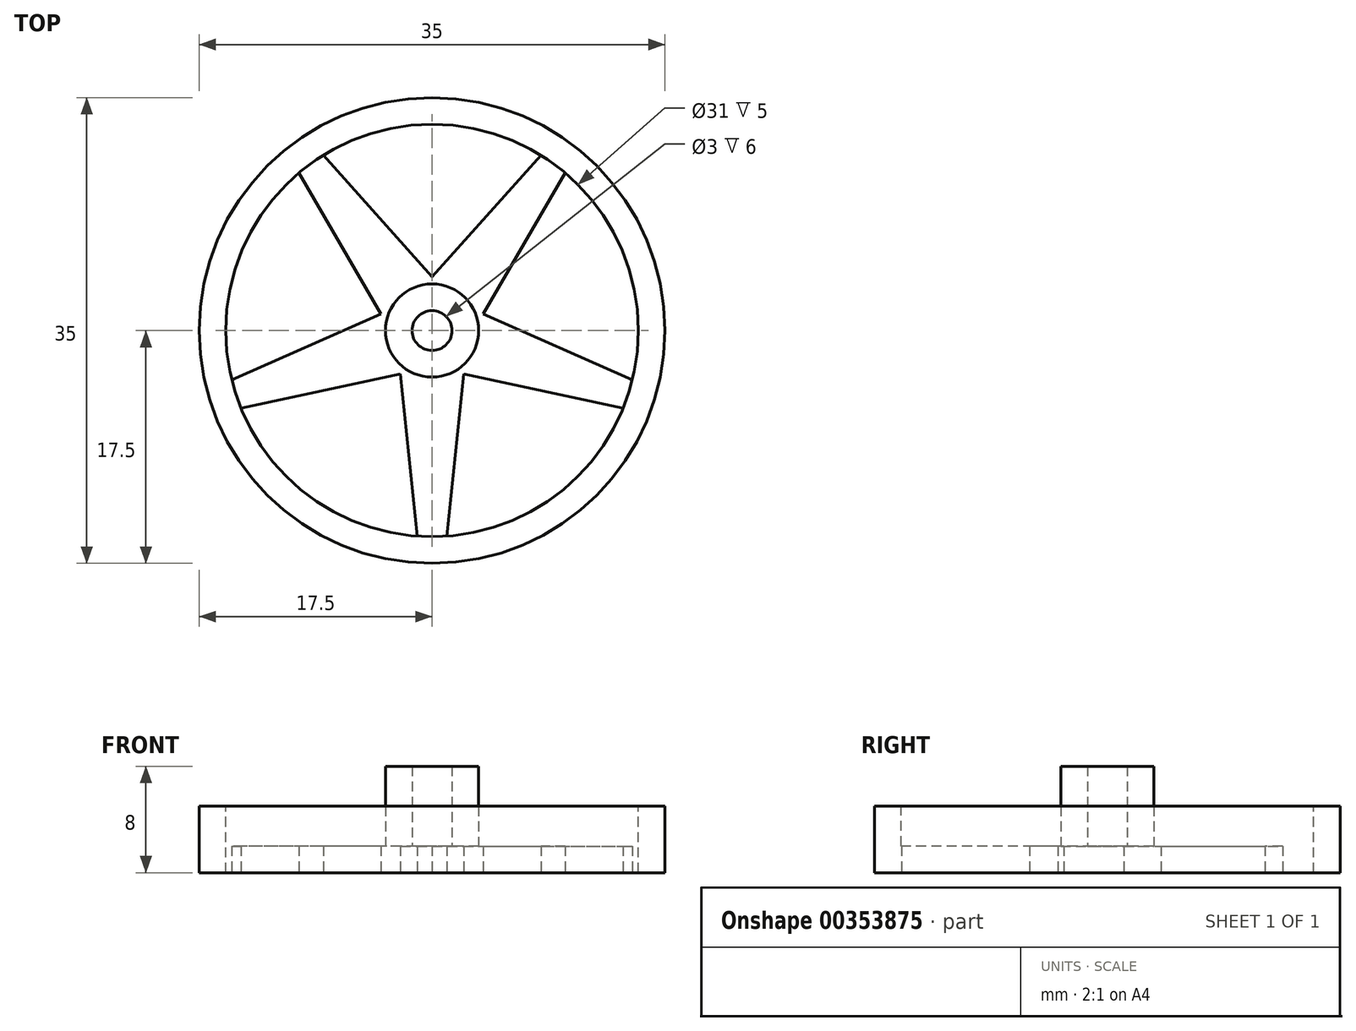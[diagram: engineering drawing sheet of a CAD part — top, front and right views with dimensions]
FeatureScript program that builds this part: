
annotation { "Feature Type Name" : "Feature", "Feature Type Description" : "" }
export const myFeature = defineFeature(function(context is Context, id is Id, definition is map)
    precondition{}
    {
        {
            var Q0;
            Q0=qCreatedBy(makeId("Top.planeOp"),FACE);
            var sketch = newSketch(context, id + "F0", { "sketchPlane" : qUnion([Q0])});
            skCircle(sketch, "E0", {"center": v(0, 0) * mm, "radius": 17.5 * mm});
            skSolve(sketch);
        }
        {
            var Q0;
            Q0=makeQuery(id+"F0.imprint","IMPRINT",FACE,{"disambiguationData":[TD([[makeQuery(id+"F0.imprint","IMPRINT",EDGE,{"derivedFrom":sQuery(id+"F0.wireOp",EDGE,"E0")}),1.0]])]});
            extrude(context, id + "F1", {"entities" : qUnion([Q0]), "depth" : 5 * mm});
        }
        {
            var Q0;
            Q0=makeQuery(id+"F1.opExtrude","CAP_FACE",FACE,{"disambiguationData":[OSD([sQuery(id+"F0.wireOp",EDGE,"E0")])],"isStart":false});
            var sketch = newSketch(context, id + "F2", { "sketchPlane" : qUnion([Q0])});
            skCircle(sketch, "E1", {"center": v(0, 0) * mm, "radius": 15.5 * mm});
            skSolve(sketch);
        }
        {
            var Q0;
            Q0=makeQuery(id+"F2.imprint","IMPRINT",FACE,{"disambiguationData":[TD([[makeQuery(id+"F2.imprint","IMPRINT",EDGE,{"derivedFrom":sQuery(id+"F2.wireOp",EDGE,"E1")}),1.0]])]});
            extrude(context, id + "F3", {"entities" : qUnion([Q0]), "operationType" : NewBodyOperationType.REMOVE, "oppositeDirection" : true, "depth" : 3 * mm});
        }
        {
            var Q0;
            Q0=makeQuery(id+"F3.boolean.opBoolean","COPY",FACE,{"derivedFrom":makeQuery(id+"F3.opExtrude","CAP_FACE",FACE,{"disambiguationData":[OSD([sQuery(id+"F2.wireOp",EDGE,"E1")])],"isStart":false})});
            var sketch = newSketch(context, id + "F4", { "sketchPlane" : qUnion([Q0])});
            skCircle(sketch, "E2", {"center": v(0, 0) * mm, "radius": 3.5 * mm});
            skCircle(sketch, "E3", {"center": v(0, 0) * mm, "radius": 1.5 * mm});
            skSolve(sketch);
        }
        {
            var Q0;
            Q0=makeQuery(id+"F4.imprint","IMPRINT",FACE,{"disambiguationData":[TD([[makeQuery(id+"F4.imprint","IMPRINT",EDGE,{"derivedFrom":sQuery(id+"F4.wireOp",EDGE,"E2")}),1.0]])]});
            extrude(context, id + "F5", {"entities" : qUnion([Q0]), "operationType" : NewBodyOperationType.ADD, "depth" : 6 * mm});
        }
        {
            var Q0;
            Q0=makeQuery(id+"F1.opExtrude","CAP_FACE",FACE,{"disambiguationData":[OSD([sQuery(id+"F0.wireOp",EDGE,"E0")])],"isStart":true});
            var sketch = newSketch(context, id + "F6", { "sketchPlane" : qUnion([Q0])});
            skCircle(sketch, "E4", {"center": v(0, 0) * mm, "radius": 3.5 * mm});
            skCircle(sketch, "E5", {"center": v(0, 0) * mm, "radius": 15.5 * mm});
            skLineSegment(sketch, "E6", {"start": v(-2.45, 2.5) * mm, "end": v(-1.12, 15.46) * mm});
            skLineSegment(sketch, "E7.MirrorCS", {"start": v(2.45, 2.5) * mm, "end": v(1.12, 15.46) * mm});
            skLineSegment(sketch, "E8.1.0", {"start": v(-1.62, 3.1) * mm, "end": v(-14.36, 5.85) * mm});
            skLineSegment(sketch, "E8.1.1", {"start": v(-3.13, -1.56) * mm, "end": v(-15.05, 3.7) * mm});
            skLineSegment(sketch, "E8.2.0", {"start": v(-3.45, -0.58) * mm, "end": v(-10, -11.85) * mm});
            skLineSegment(sketch, "E8.2.1", {"start": v(0.51, -3.46) * mm, "end": v(-8.18, -13.17) * mm});
            skLineSegment(sketch, "E8.3.0", {"start": v(-0.51, -3.46) * mm, "end": v(8.18, -13.17) * mm});
            skLineSegment(sketch, "E8.3.1", {"start": v(3.45, -0.58) * mm, "end": v(10, -11.85) * mm});
            skLineSegment(sketch, "E8.4.0", {"start": v(3.13, -1.56) * mm, "end": v(15.05, 3.7) * mm});
            skLineSegment(sketch, "E8.4.1", {"start": v(1.62, 3.1) * mm, "end": v(14.36, 5.85) * mm});
            skSolve(sketch);
        }
        {
            var Q0;
            {var subQ0=sQuery(id+"F6.wireOp",EDGE,"E6");var subQ1=sQuery(id+"F6.wireOp",EDGE,"E5");var subQ2=makeQuery(id+"F6.imprint","INTERSECT",VERTEX,{"derivedFrom":[subQ1,subQ0]});Q0=makeQuery(id+"F6.imprint","IMPRINT",FACE,{"disambiguationData":[TD([[makeQuery(id+"F6.imprint","IMPRINT",EDGE,{"disambiguationData":[TD([[subQ2,-1.0]])],"derivedFrom":subQ1}),1.0]])]});}
            var Q1;
            {var subQ0=sQuery(id+"F6.wireOp",EDGE,"E7.MirrorCS");var subQ1=sQuery(id+"F6.wireOp",EDGE,"E5");var subQ2=makeQuery(id+"F6.imprint","INTERSECT",VERTEX,{"derivedFrom":[subQ1,subQ0]});Q1=makeQuery(id+"F6.imprint","IMPRINT",FACE,{"disambiguationData":[TD([[makeQuery(id+"F6.imprint","IMPRINT",EDGE,{"disambiguationData":[TD([[subQ2,1.0]])],"derivedFrom":subQ1}),1.0]])]});}
            var Q2;
            {var subQ0=sQuery(id+"F6.wireOp",EDGE,"E8.3.1");var subQ1=sQuery(id+"F6.wireOp",EDGE,"E5");var subQ2=makeQuery(id+"F6.imprint","INTERSECT",VERTEX,{"derivedFrom":[subQ1,subQ0]});Q2=makeQuery(id+"F6.imprint","IMPRINT",FACE,{"disambiguationData":[TD([[makeQuery(id+"F6.imprint","IMPRINT",EDGE,{"disambiguationData":[TD([[subQ2,-1.0]])],"derivedFrom":subQ1}),1.0]])]});}
            var Q3;
            {var subQ0=sQuery(id+"F6.wireOp",EDGE,"E8.2.1");var subQ1=sQuery(id+"F6.wireOp",EDGE,"E5");var subQ2=makeQuery(id+"F6.imprint","INTERSECT",VERTEX,{"derivedFrom":[subQ1,subQ0]});Q3=makeQuery(id+"F6.imprint","IMPRINT",FACE,{"disambiguationData":[TD([[makeQuery(id+"F6.imprint","IMPRINT",EDGE,{"disambiguationData":[TD([[subQ2,-1.0]])],"derivedFrom":subQ1}),1.0]])]});}
            var Q4;
            {var subQ0=sQuery(id+"F6.wireOp",EDGE,"E8.1.1");var subQ1=sQuery(id+"F6.wireOp",EDGE,"E5");var subQ2=makeQuery(id+"F6.imprint","INTERSECT",VERTEX,{"derivedFrom":[subQ1,subQ0]});Q4=makeQuery(id+"F6.imprint","IMPRINT",FACE,{"disambiguationData":[TD([[makeQuery(id+"F6.imprint","IMPRINT",EDGE,{"disambiguationData":[TD([[subQ2,-1.0]])],"derivedFrom":subQ1}),1.0]])]});}
            extrude(context, id + "F7", {"entities" : qUnion([Q0, Q1, Q2, Q3, Q4]), "operationType" : NewBodyOperationType.REMOVE, "oppositeDirection" : true, "depth" : 2 * mm});
        }
    });
